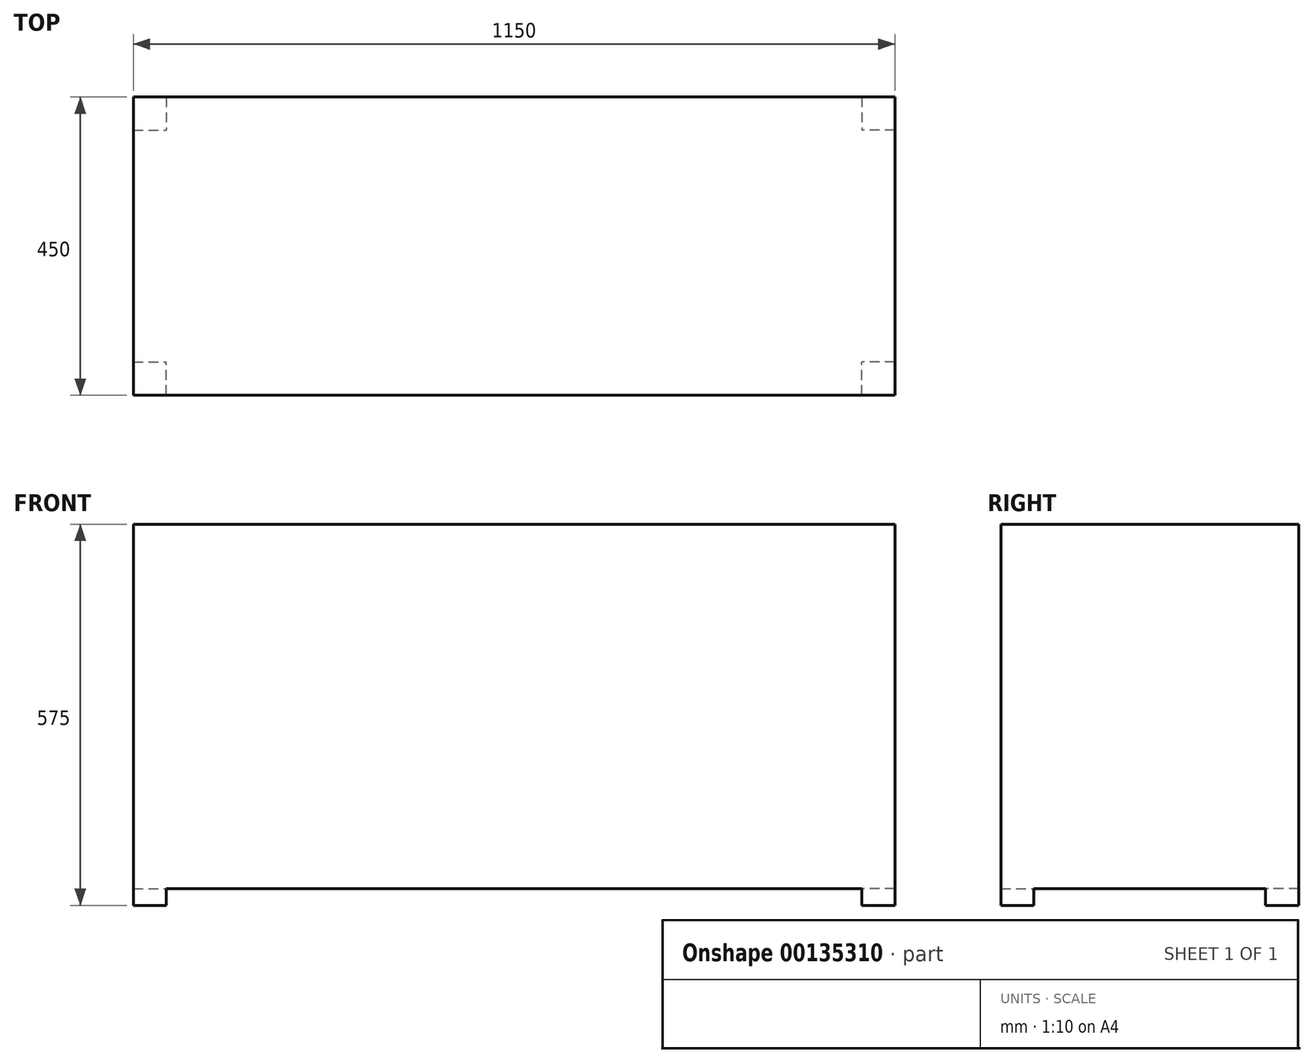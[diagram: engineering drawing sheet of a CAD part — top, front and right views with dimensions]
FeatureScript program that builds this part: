
annotation { "Feature Type Name" : "Feature", "Feature Type Description" : "" }
export const myFeature = defineFeature(function(context is Context, id is Id, definition is map)
    precondition{}
    {
        {
            var Q0;
            Q0=qCreatedBy(makeId("Top.planeOp"),FACE);
            var sketch = newSketch(context, id + "F0", { "sketchPlane" : qUnion([Q0])});
            skLineSegment(sketch, "E0.bottom", {"start": v(-575, 225) * mm, "end": v(575, 225) * mm});
            skLineSegment(sketch, "E0.top", {"start": v(-575, -225) * mm, "end": v(575, -225) * mm});
            skLineSegment(sketch, "E0.left", {"start": v(-575, 225) * mm, "end": v(-575, -225) * mm});
            skLineSegment(sketch, "E0.right", {"start": v(575, 225) * mm, "end": v(575, -225) * mm});
            skPoint(sketch, "E0.middle", {"position": v(0, 0) * mm});
            skSolve(sketch);
        }
        {
            var Q0;
            Q0 = qSketchRegion(id + "F0", true);
            extrude(context, id + "F1", {"entities" : qUnion([Q0]), "depth" : 550 * mm});
        }
        {
            var Q0;
            Q0=makeQuery(id+"F1.opExtrude","CAP_FACE",FACE,{"disambiguationData":[OSD([sQuery(id+"F0.wireOp",EDGE,"E0.bottom"),sQuery(id+"F0.wireOp",EDGE,"E0.top"),sQuery(id+"F0.wireOp",EDGE,"E0.left"),sQuery(id+"F0.wireOp",EDGE,"E0.right")])],"isStart":true});
            var sketch = newSketch(context, id + "F2", { "sketchPlane" : qUnion([Q0])});
            skLineSegment(sketch, "E1.bottom", {"start": v(575, 225) * mm, "end": v(525, 225) * mm});
            skLineSegment(sketch, "E1.top", {"start": v(575, 175) * mm, "end": v(525, 175) * mm});
            skLineSegment(sketch, "E1.left", {"start": v(575, 225) * mm, "end": v(575, 175) * mm});
            skLineSegment(sketch, "E1.right", {"start": v(525, 225) * mm, "end": v(525, 175) * mm});
            skLineSegment(sketch, "E2.MirrorCS", {"start": v(-575, 225) * mm, "end": v(-525, 225) * mm});
            skLineSegment(sketch, "E3.MirrorCS", {"start": v(-575, 175) * mm, "end": v(-525, 175) * mm});
            skLineSegment(sketch, "E4.MirrorCS", {"start": v(-525, 225) * mm, "end": v(-525, 175) * mm});
            skLineSegment(sketch, "E5.MirrorCS", {"start": v(-575, 225) * mm, "end": v(-575, 175) * mm});
            skLineSegment(sketch, "E6.MirrorCS", {"start": v(575, -225) * mm, "end": v(575, -175) * mm});
            skLineSegment(sketch, "E7.MirrorCS", {"start": v(-575, -225) * mm, "end": v(-525, -225) * mm});
            skLineSegment(sketch, "E8.MirrorCS", {"start": v(-575, -175) * mm, "end": v(-525, -175) * mm});
            skLineSegment(sketch, "E9.MirrorCS", {"start": v(-575, -225) * mm, "end": v(-575, -175) * mm});
            skLineSegment(sketch, "E10.MirrorCS", {"start": v(525, -225) * mm, "end": v(525, -175) * mm});
            skLineSegment(sketch, "E11.MirrorCS", {"start": v(575, -175) * mm, "end": v(525, -175) * mm});
            skLineSegment(sketch, "E12.MirrorCS", {"start": v(575, -225) * mm, "end": v(525, -225) * mm});
            skLineSegment(sketch, "E13.MirrorCS", {"start": v(-525, -225) * mm, "end": v(-525, -175) * mm});
            skSolve(sketch);
        }
        {
            var Q0;
            Q0 = qSketchRegion(id + "F2", true);
            extrude(context, id + "F3", {"entities" : qUnion([Q0]), "operationType" : NewBodyOperationType.ADD, "depth" : 25 * mm});
        }
    });
